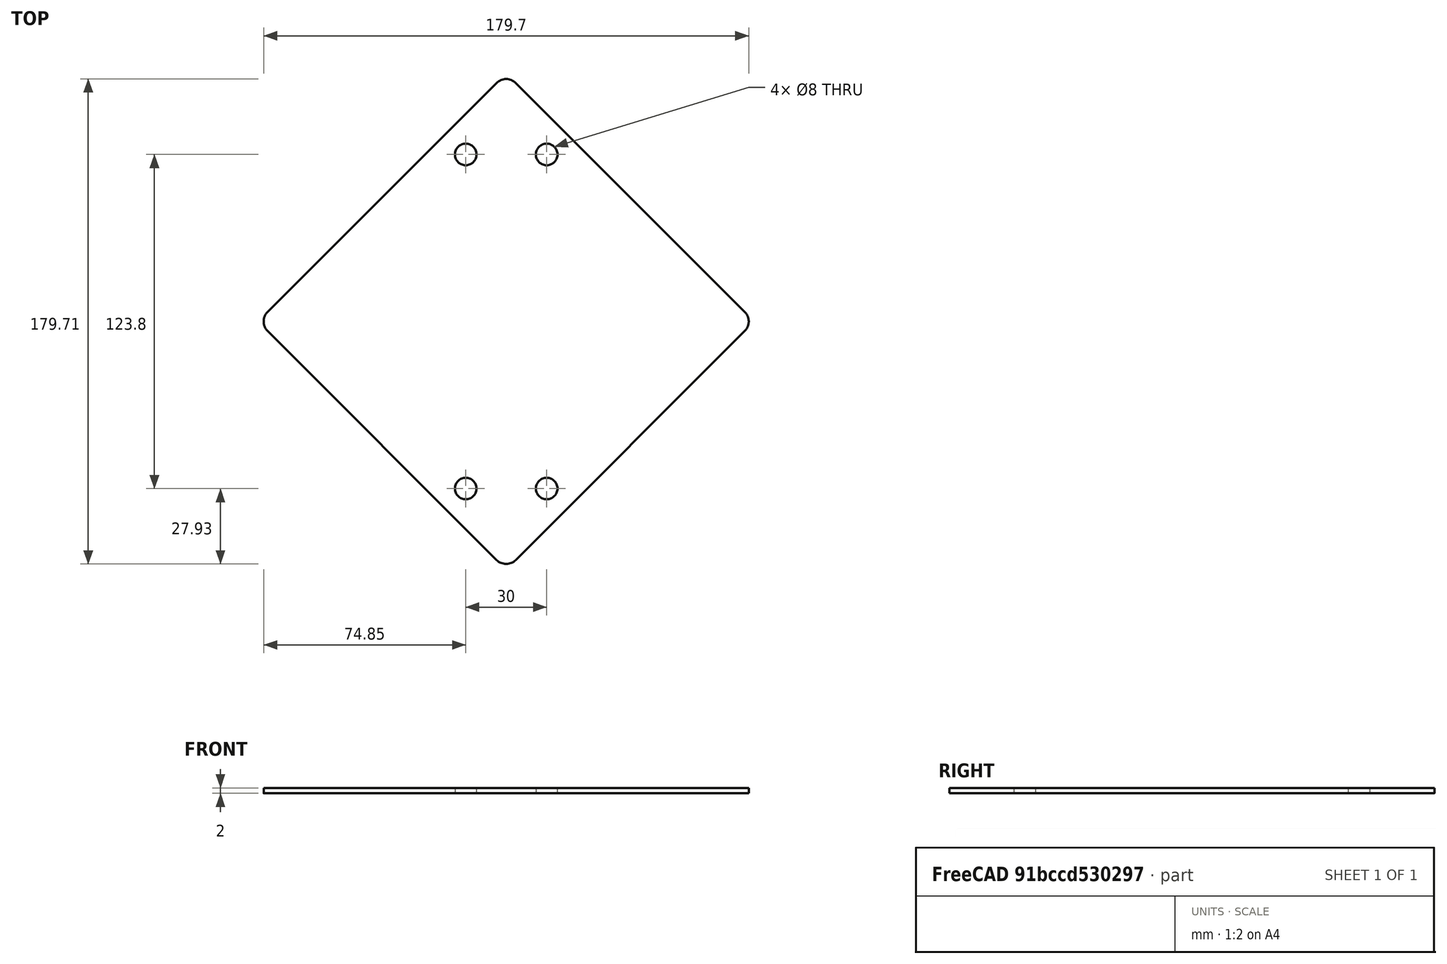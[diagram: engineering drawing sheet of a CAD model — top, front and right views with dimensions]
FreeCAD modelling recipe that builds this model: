
FCSTD DOCUMENT  (FreeCAD 0.20R29177 +426 (Git))
Label: Osnova_Logo
License: All rights reserved
LicenseURL: http://en.wikipedia.org/wiki/All_rights_reserved
objects: Part::Cylinder×4, Part::Box×1, Part::Fillet×1, Part::MultiFuse×1, Part::Cut×1
note: 8 computed .brp shape members not serialized (recipe doc carries the construction recipe); baked Part::Feature solids carry a one-line shape summary decoded from their .brp

FEATURE [Part::Box] Box  label="Cube"
  AttacherType = Attacher::AttachEngine3D
  Height = 2
  Length = 130
  Width = 130
FEATURE [Part::Fillet] Fillet
  Base = -> Box
  Edges = 4 edges r=5: [Edge1,Edge3,Edge5,Edge7]
  Placement = pos=(0,0,0) rot=(0,0,1;0.785398rad)
FEATURE [Part::Cylinder] Cylinder
  Angle = 360
  AttacherType = Attacher::AttachEngine3D
  FirstAngle = 0
  Height = 10
  Placement = pos=(15,30,0) rot=(0,0,1;0rad)
  Radius = 4
  SecondAngle = 0
FEATURE [Part::Cylinder] Cylinder001
  Angle = 360
  AttacherType = Attacher::AttachEngine3D
  FirstAngle = 0
  Height = 10
  Placement = pos=(-15,30,0) rot=(0,0,1;0rad)
  Radius = 4
  SecondAngle = 0
FEATURE [Part::Cylinder] Cylinder002
  Angle = 360
  AttacherType = Attacher::AttachEngine3D
  FirstAngle = 0
  Height = 10
  Placement = pos=(-15,153.8,0) rot=(0,0,1;0rad)
  Radius = 4
  SecondAngle = 0
FEATURE [Part::Cylinder] Cylinder003
  Angle = 360
  AttacherType = Attacher::AttachEngine3D
  FirstAngle = 0
  Height = 10
  Placement = pos=(15,153.8,0) rot=(0,0,1;0rad)
  Radius = 4
  SecondAngle = 0
FEATURE [Part::MultiFuse] Fusion
  Shapes = -> [Cylinder003,Cylinder,Cylinder001,Cylinder002]
FEATURE [Part::Cut] Cut
  Base = -> Fillet
  Tool = -> Fusion
